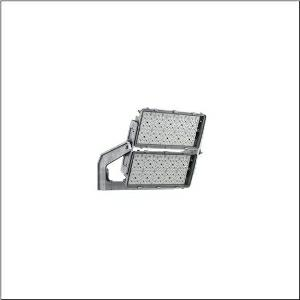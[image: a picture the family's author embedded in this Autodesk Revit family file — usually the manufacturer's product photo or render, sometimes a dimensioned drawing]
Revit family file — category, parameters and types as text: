
# Revit family: floodlight_fl_11_maxi_remote___rs12_5xa779514m01aa_cc46
name_source: partatom
category: Lighting Fixtures
units: mm (PartAtom-declared; Revit-internal decimal feet)

## family parameters
Cut with Voids When Loaded = No
Host = Face
Light Source = No
Part Type = Normal
Room Calculation Point = No
Round Connector Dimension = Use Diameter
Shared = No

## types (1)
- --- (1 x LED, 90180 lm, 916.8 W, 5700K)
    Apparent Load = 917 VA
    CIE Flux Codes = 79 92 99 100 100
    Color Rendering = 90
    Color Temperature = 5700K
    Default Elevation = 1800 mm
    Description = Floodlight FL 11  maxi  Remote floodlight; light control with lens of PMMA; cover panel of toughened safety glass, transparent; light distribution: RS12, rotationally symmetric direct distribution, LEDcolour temperature: 5700K, rated luminous flux: 90.180lm, colour rendering: CRI > 90, light colour: 957; luminous efficacy: 98lm/W; brightness control: DMX+RDM; with terminal, 6-pole, max. 2.5mm², mains connection: 220..240V/380..400V AC, 50/60Hz, surge voltage resistance: line to ground: 10kV, ECG replaceable separately, no afterglow with DALI off / DMX off command, LED unit replaceable without ESD environment, dustproof LED module, dimming range 10..100%; 917W floodlight with 2x LED unit of diecast aluminium, coated grey; length: 713mm / width: 651mm / height: 338mm; mounting bracket, of diecast aluminium, uncoated, natural, equipment: Power, protection rating (complete): IP66; insulation class (complete): insulation class I (protective earthing); certification: CE, ENEC, VDE; ball protection: ball impact resistance with accessories, impact resistance: IK07; rated ambient temperature 10°C, only for outdoor installations, permissible operating ambient temperature: -40..+30°C, permissible storage temperature: -40..+85°Cpackaging unit: 1 piece

Light Distribution: RS12
    Height = 320 mm
    Lamp = 1 x LED
    Lamp Light Flux = 90180 lm
    Lamp Power = 916.8 W
    Lamp count = 1
    Length = 712 mm
    Luminous efficacy = 98 lm/W
    Manufacturer = Siteco
    ModVariant = No
    Model = 5XA779514M01AA
    Mounting Place = Ceiling
    Mounting Type = Surface mounted
    Number of Poles = 1
    OnlyDefault = Yes
    Power Factor = 1
    Product Name = Floodlight FL 11 maxi Remote | RS12
    Product group = floodlight | ceiling mounted
    ProductGroupID = 301
    Protection Class = Protection class I
    Protection Degree = IP 66
    RLX_Detail_Level = 1
    RLX_Emergency_Light_Flux = 0 lm
    RLX_Emergency_Type = 0
    RLX_Emergency_Type_DB = No
    RlxData = <blob elided: 40997 chars, md5=6a9b8c3f>
    Socket = socket
    Standby Power = 0 W
    System Light Flux = 90180 lm
    System Power = 917 W
    Type Comments = factory setting: luminous flux: 100 % | dim-lin: 254 | 950 mA
    Type Image = l_1349125.jpg
    URL = http://relux.com
    VarID = @adj_182092
    Voltage = 0 V
    Weight = 0.00 kg
    Width = 655 mm

## geometry (parser evidence)
native form markers: Blend x4, Sweep x14
no freeform markers — native parametric forms only
